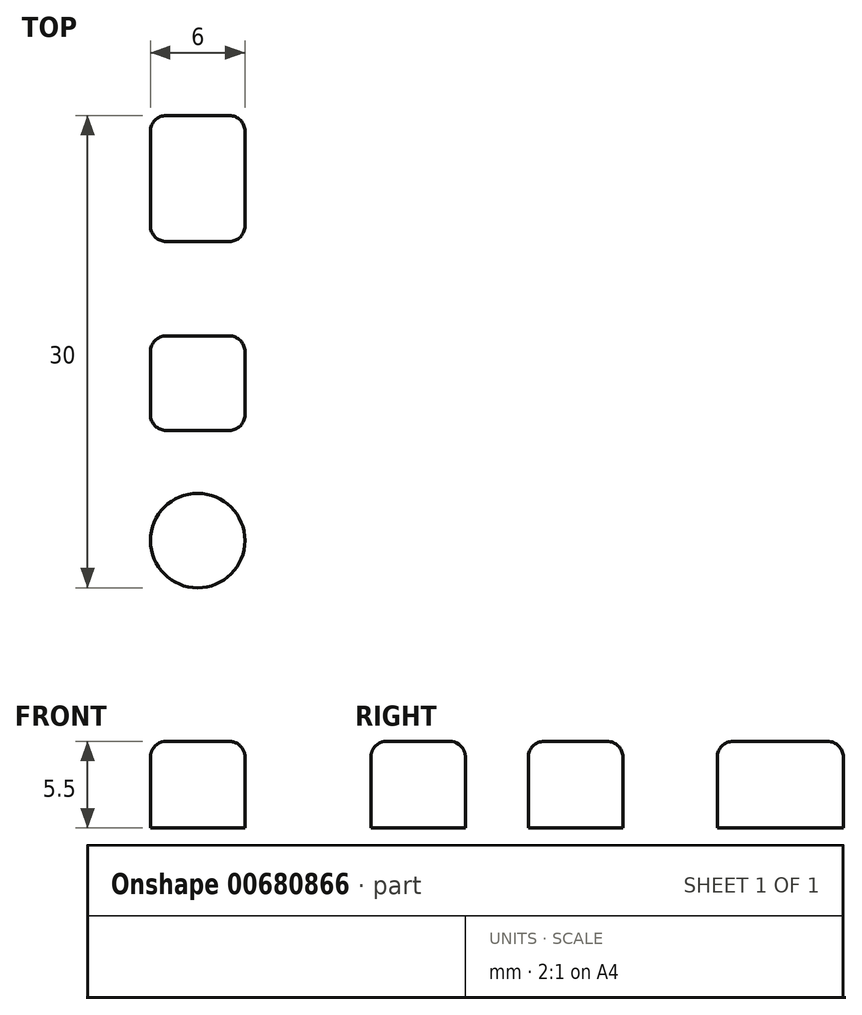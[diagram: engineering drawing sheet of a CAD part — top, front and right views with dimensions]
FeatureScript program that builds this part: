
annotation { "Feature Type Name" : "Feature", "Feature Type Description" : "" }
export const myFeature = defineFeature(function(context is Context, id is Id, definition is map)
    precondition{}
    {
        {
            var Q0;
            Q0=qCreatedBy(makeId("Top.planeOp"),FACE);
            var sketch = newSketch(context, id + "F0", { "sketchPlane" : qUnion([Q0])});
            skLineSegment(sketch, "E0.bottom", {"start": v(-2, 0) * mm, "end": v(2, 0) * mm});
            skLineSegment(sketch, "E0.top", {"start": v(-2, -8) * mm, "end": v(2, -8) * mm});
            skLineSegment(sketch, "E0.left", {"start": v(-3, -1) * mm, "end": v(-3, -7) * mm});
            skLineSegment(sketch, "E0.right", {"start": v(3, -1) * mm, "end": v(3, -7) * mm});
            skLineSegment(sketch, "E1.bottom", {"start": v(-2, -14) * mm, "end": v(2, -14) * mm});
            skLineSegment(sketch, "E1.top", {"start": v(-2, -20) * mm, "end": v(2, -20) * mm});
            skLineSegment(sketch, "E1.left", {"start": v(-3, -15) * mm, "end": v(-3, -19) * mm});
            skLineSegment(sketch, "E1.right", {"start": v(3, -15) * mm, "end": v(3, -19) * mm});
            skCircle(sketch, "E2", {"center": v(0, -27) * mm, "radius": 3 * mm});
            skPoint(sketch, "E3.visualSharp", {"position": v(-3, -8) * mm});
            skArc(sketch, "E3.filletArc", {"start": v(-3, -7) * mm, "mid": v(-2.7, -7.7) * mm, "end": v(-2, -8) * mm});
            skPoint(sketch, "E4.visualSharp", {"position": v(-3, 0) * mm});
            skArc(sketch, "E4.filletArc", {"start": v(-2, 0) * mm, "mid": v(-2.7, -0.3) * mm, "end": v(-3, -1) * mm});
            skPoint(sketch, "E5.visualSharp", {"position": v(3, 0) * mm});
            skArc(sketch, "E5.filletArc", {"start": v(3, -1) * mm, "mid": v(2.7, -0.3) * mm, "end": v(2, 0) * mm});
            skPoint(sketch, "E6.visualSharp", {"position": v(3, -8) * mm});
            skArc(sketch, "E6.filletArc", {"start": v(2, -8) * mm, "mid": v(2.7, -7.7) * mm, "end": v(3, -7) * mm});
            skPoint(sketch, "E7.visualSharp", {"position": v(-3, -14) * mm});
            skArc(sketch, "E7.filletArc", {"start": v(-2, -14) * mm, "mid": v(-2.7, -14.3) * mm, "end": v(-3, -15) * mm});
            skPoint(sketch, "E8.visualSharp", {"position": v(-3, -20) * mm});
            skArc(sketch, "E8.filletArc", {"start": v(-3, -19) * mm, "mid": v(-2.7, -19.7) * mm, "end": v(-2, -20) * mm});
            skPoint(sketch, "E9.visualSharp", {"position": v(3, -14) * mm});
            skArc(sketch, "E9.filletArc", {"start": v(3, -15) * mm, "mid": v(2.7, -14.3) * mm, "end": v(2, -14) * mm});
            skPoint(sketch, "E10.visualSharp", {"position": v(3, -20) * mm});
            skArc(sketch, "E10.filletArc", {"start": v(2, -20) * mm, "mid": v(2.7, -19.7) * mm, "end": v(3, -19) * mm});
            skSolve(sketch);
        }
        {
            var Q0;
            Q0=makeQuery(id+"F0.imprint","IMPRINT",FACE,{"disambiguationData":[TD([[makeQuery(id+"F0.imprint","IMPRINT",EDGE,{"derivedFrom":sQuery(id+"F0.wireOp",EDGE,"E0.bottom")}),-1.0]])]});
            extrude(context, id + "F1", {"entities" : qUnion([Q0]), "depth" : 5.5 * mm, "offsetDistance" : 25 * mm});
        }
        {
            var Q0;
            Q0=makeQuery(id+"F0.imprint","IMPRINT",FACE,{"disambiguationData":[TD([[makeQuery(id+"F0.imprint","IMPRINT",EDGE,{"derivedFrom":sQuery(id+"F0.wireOp",EDGE,"E1.bottom")}),-1.0]])]});
            var Q1;
            Q1=makeQuery(id+"F0.imprint","IMPRINT",FACE,{"disambiguationData":[TD([[makeQuery(id+"F0.imprint","IMPRINT",EDGE,{"derivedFrom":sQuery(id+"F0.wireOp",EDGE,"E2")}),1.0]])]});
            extrude(context, id + "F2", {"entities" : qUnion([Q0, Q1]), "depth" : 5.5 * mm, "offsetDistance" : 25 * mm});
        }
        {
            var Q0;
            Q0=makeQuery(id+"F2.opExtrude","CAP_EDGE",EDGE,{"disambiguationData":[OSD([sQuery(id+"F0.wireOp",EDGE,"E2")])],"isStart":false});
            fillet(context, id + "F3", {"entities" : qUnion([Q0]), "radius" : 1 * mm, "tangentPropagation" : true, "allowEdgeOverflow" : false});
        }
        {
            var Q0;
            Q0=makeQuery(id+"F2.opExtrude","CAP_FACE",FACE,{"disambiguationData":[OSD([sQuery(id+"F0.wireOp",EDGE,"E1.bottom"),sQuery(id+"F0.wireOp",EDGE,"E1.top"),sQuery(id+"F0.wireOp",EDGE,"E1.left"),sQuery(id+"F0.wireOp",EDGE,"E1.right")])],"isStart":false});
            fillet(context, id + "F4", {"entities" : qUnion([Q0]), "radius" : 1 * mm, "tangentPropagation" : true, "allowEdgeOverflow" : false});
        }
        {
            var Q0;
            Q0=makeQuery(id+"F1.opExtrude","CAP_FACE",FACE,{"disambiguationData":[OSD([sQuery(id+"F0.wireOp",EDGE,"E0.bottom"),sQuery(id+"F0.wireOp",EDGE,"E0.top"),sQuery(id+"F0.wireOp",EDGE,"E0.left"),sQuery(id+"F0.wireOp",EDGE,"E0.right")])],"isStart":false});
            fillet(context, id + "F5", {"entities" : qUnion([Q0]), "radius" : 1 * mm, "tangentPropagation" : true, "allowEdgeOverflow" : false});
        }
    });
